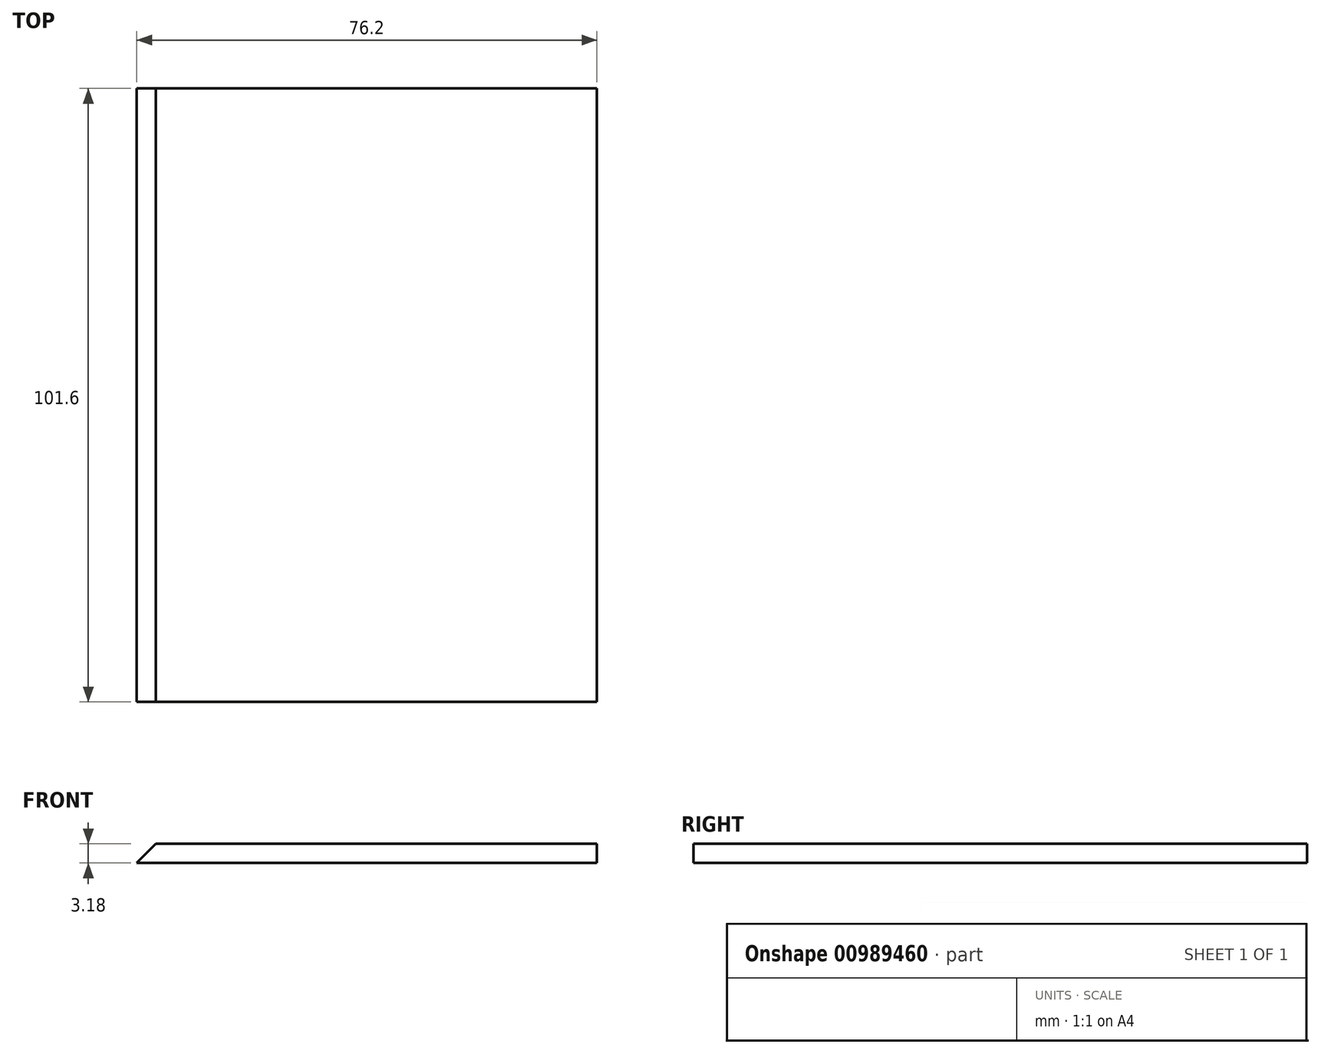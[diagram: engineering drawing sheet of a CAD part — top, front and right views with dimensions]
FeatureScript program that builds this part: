
annotation { "Feature Type Name" : "Feature", "Feature Type Description" : "" }
export const myFeature = defineFeature(function(context is Context, id is Id, definition is map)
    precondition{}
    {
        {
            var Q0;
            Q0=qCreatedBy(makeId("Front.planeOp"),FACE);
            var sketch = newSketch(context, id + "F0", { "sketchPlane" : qUnion([Q0])});
            skLineSegment(sketch, "E0.bottom", {"start": v(38.1, 1.59) * mm, "end": v(-34.92, 1.59) * mm});
            skLineSegment(sketch, "E0.top", {"start": v(38.1, -1.59) * mm, "end": v(-38.1, -1.59) * mm});
            skLineSegment(sketch, "E0.left", {"start": v(38.1, 1.59) * mm, "end": v(38.1, -1.59) * mm});
            skPoint(sketch, "E0.middle", {"position": v(0, 0) * mm});
            skLineSegment(sketch, "E1", {"start": v(-38.1, -1.59) * mm, "end": v(-34.92, 1.59) * mm});
            skPoint(sketch, "E2.orphan", {"position": v(-38.1, 1.59) * mm});
            skSolve(sketch);
        }
        {
            var Q0;
            Q0 = qSketchRegion(id + "F0", true);
            extrude(context, id + "F1", {"entities" : qUnion([Q0]), "endBound" : BoundingType.SYMMETRIC, "depth" : 101.6 * mm, "offsetDistance" : 25.4 * mm});
        }
    });
